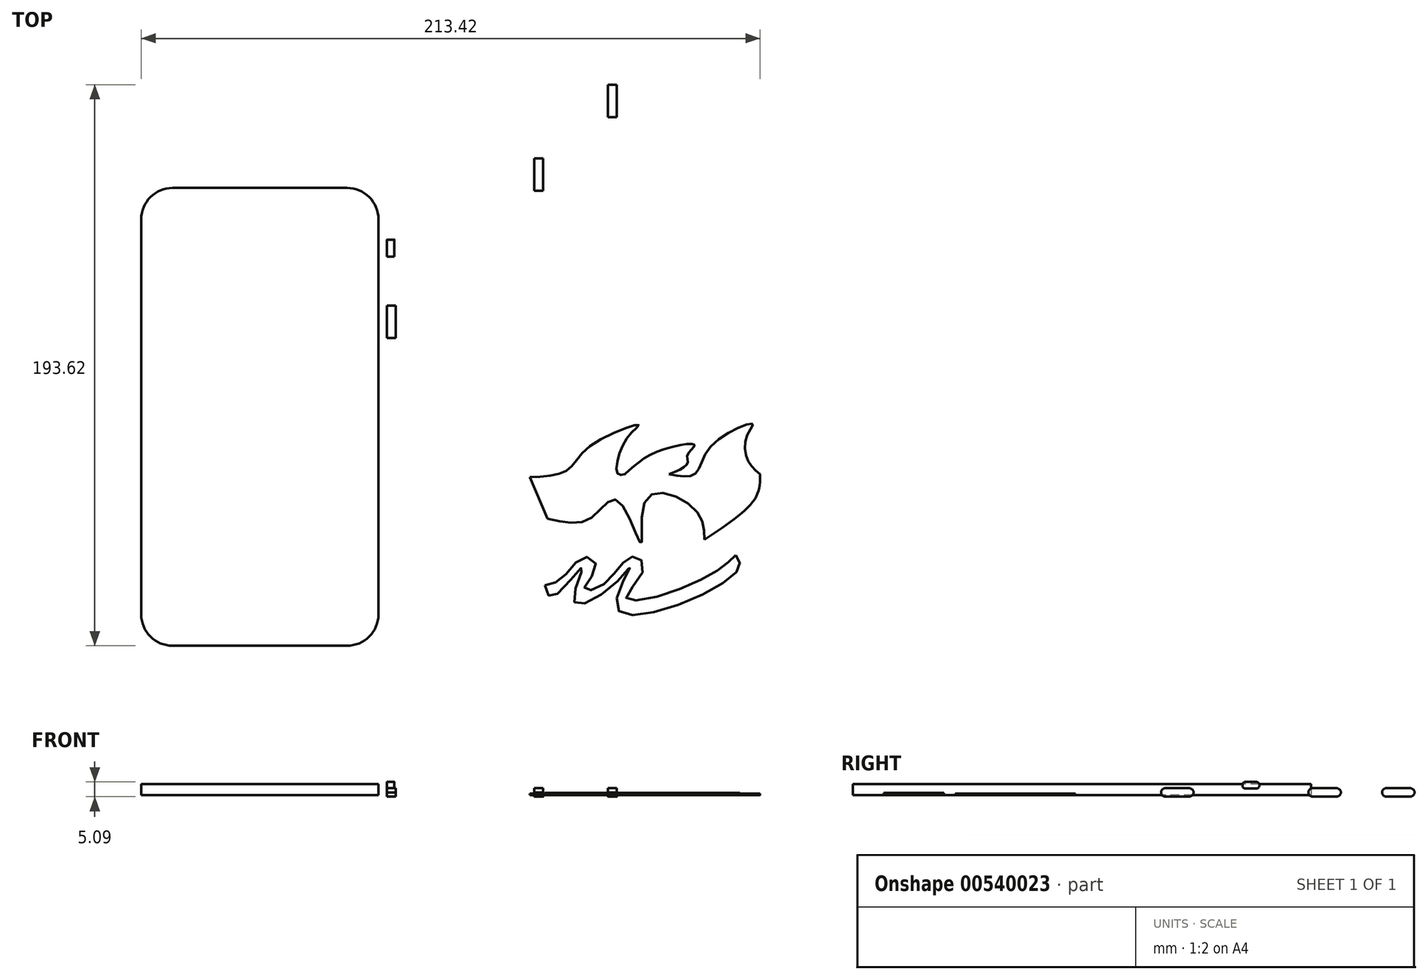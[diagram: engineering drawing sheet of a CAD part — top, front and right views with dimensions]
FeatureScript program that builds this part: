
annotation { "Feature Type Name" : "Feature", "Feature Type Description" : "" }
export const myFeature = defineFeature(function(context is Context, id is Id, definition is map)
    precondition{}
    {
        {
            var Q0;
            Q0=qCreatedBy(makeId("Right.planeOp"),FACE);
            var sketch = newSketch(context, id + "F0", { "sketchPlane" : qUnion([Q0])});
            skLineSegment(sketch, "E0.bottom", {"start": v(8.18, 2.37) * mm, "end": v(16.31, 2.37) * mm});
            skLineSegment(sketch, "E0.top", {"start": v(8.18, -0.57) * mm, "end": v(16.31, -0.57) * mm});
            skPoint(sketch, "E1.visualSharp", {"position": v(6.63, 2.37) * mm});
            skArc(sketch, "E1.filletArc", {"start": v(8.18, 2.37) * mm, "mid": v(7.09, 1.92) * mm, "end": v(6.63, 0.82) * mm});
            skPoint(sketch, "E2.visualSharp", {"position": v(17.86, 2.37) * mm});
            skArc(sketch, "E2.filletArc", {"start": v(17.86, 0.82) * mm, "mid": v(17.4, 1.92) * mm, "end": v(16.31, 2.37) * mm});
            skPoint(sketch, "E3.visualSharp", {"position": v(6.63, -0.57) * mm});
            skArc(sketch, "E3.filletArc", {"start": v(6.63, 0.98) * mm, "mid": v(7.09, -0.12) * mm, "end": v(8.18, -0.57) * mm});
            skPoint(sketch, "E4.visualSharp", {"position": v(17.86, -0.57) * mm});
            skArc(sketch, "E4.filletArc", {"start": v(16.31, -0.57) * mm, "mid": v(17.4, -0.12) * mm, "end": v(17.86, 0.98) * mm});
            skSolve(sketch);
        }
        {
            var Q0;
            Q0 = qSketchRegion(id + "F0", true);
            extrude(context, id + "F1", {"entities" : qUnion([Q0]), "depth" : 3.05 * mm, "offsetDistance" : 25.4 * mm});
        }
        {
            var Q0;
            Q0=makeQuery(id+"F1.opExtrude","SWEPT_BODY",BODY,{"disambiguationData":[OSD([sQuery(id+"F0.wireOp",EDGE,"E0.bottom"),sQuery(id+"F0.wireOp",EDGE,"E0.top"),sQuery(id+"F0.wireOp",EDGE,"E1.filletArc"),sQuery(id+"F0.wireOp",EDGE,"E2.filletArc"),sQuery(id+"F0.wireOp",EDGE,"E3.filletArc"),sQuery(id+"F0.wireOp",EDGE,"E4.filletArc")])]});
            transform(context, id + "F2", {"entities" : qUnion([Q0]), "transformType" : TransformType.TRANSLATION_3D, "dx" : 50.8 * mm, "dy" : 50.8 * mm, "dz" : 0 * mm, "makeCopy" : true});
        }
        {
            var Q0;
            Q0=makeQuery(id+"F2.opPattern","COPY",BODY,{"derivedFrom":makeQuery(id+"F1.opExtrude","SWEPT_BODY",BODY,{"disambiguationData":[OSD([sQuery(id+"F0.wireOp",EDGE,"E0.bottom"),sQuery(id+"F0.wireOp",EDGE,"E0.top"),sQuery(id+"F0.wireOp",EDGE,"E1.filletArc"),sQuery(id+"F0.wireOp",EDGE,"E2.filletArc"),sQuery(id+"F0.wireOp",EDGE,"E3.filletArc"),sQuery(id+"F0.wireOp",EDGE,"E4.filletArc")])]}),"instanceName":"1"});
            transform(context, id + "F3", {"entities" : qUnion([Q0]), "transformType" : TransformType.TRANSLATION_3D, "dx" : 25.4 * mm, "dy" : 25.4 * mm, "dz" : 0 * mm, "makeCopy" : true});
        }
        {
            var Q0;
            Q0=qCreatedBy(makeId("Right.planeOp"),FACE);
            var sketch = newSketch(context, id + "F4", { "sketchPlane" : qUnion([Q0])});
            skLineSegment(sketch, "E5.bottom", {"start": v(39.52, 4.52) * mm, "end": v(35.73, 4.52) * mm});
            skLineSegment(sketch, "E5.top", {"start": v(39.52, 2.26) * mm, "end": v(35.73, 2.26) * mm});
            skLineSegment(sketch, "E5.left", {"start": v(40.57, 3.48) * mm, "end": v(40.57, 3.3) * mm});
            skLineSegment(sketch, "E5.right", {"start": v(34.7, 3.48) * mm, "end": v(34.7, 3.3) * mm});
            skPoint(sketch, "E6.visualSharp", {"position": v(40.57, 4.52) * mm});
            skArc(sketch, "E6.filletArc", {"start": v(40.57, 3.48) * mm, "mid": v(40.26, 4.21) * mm, "end": v(39.52, 4.52) * mm});
            skPoint(sketch, "E7.visualSharp", {"position": v(34.7, 4.52) * mm});
            skArc(sketch, "E7.filletArc", {"start": v(35.73, 4.52) * mm, "mid": v(35, 4.21) * mm, "end": v(34.7, 3.48) * mm});
            skPoint(sketch, "E8.visualSharp", {"position": v(34.7, 2.26) * mm});
            skArc(sketch, "E8.filletArc", {"start": v(34.7, 3.3) * mm, "mid": v(35, 2.57) * mm, "end": v(35.73, 2.26) * mm});
            skPoint(sketch, "E9.visualSharp", {"position": v(40.57, 2.26) * mm});
            skArc(sketch, "E9.filletArc", {"start": v(39.52, 2.26) * mm, "mid": v(40.26, 2.57) * mm, "end": v(40.57, 3.3) * mm});
            skSolve(sketch);
        }
        {
            var Q0;
            Q0 = qSketchRegion(id + "F4", true);
            extrude(context, id + "F5", {"entities" : qUnion([Q0]), "depth" : 2.54 * mm, "offsetDistance" : 25.4 * mm});
        }
        {
            var Q0;
            Q0=qCreatedBy(makeId("Top.planeOp"),FACE);
            var sketch = newSketch(context, id + "F6", { "sketchPlane" : qUnion([Q0])});
            skLineSegment(sketch, "E10.bottom", {"start": v(-73.9, 58.43) * mm, "end": v(-13.76, 58.43) * mm});
            skLineSegment(sketch, "E10.top", {"start": v(-73.9, -99.56) * mm, "end": v(-13.76, -99.56) * mm});
            skLineSegment(sketch, "E10.left", {"start": v(-84.73, 47.6) * mm, "end": v(-84.73, -88.74) * mm});
            skLineSegment(sketch, "E10.right", {"start": v(-2.94, 47.6) * mm, "end": v(-2.94, -88.74) * mm});
            skPoint(sketch, "E11.visualSharp", {"position": v(-84.73, 58.43) * mm});
            skArc(sketch, "E11.filletArc", {"start": v(-73.9, 58.43) * mm, "mid": v(-81.56, 55.26) * mm, "end": v(-84.73, 47.6) * mm});
            skPoint(sketch, "E12.visualSharp", {"position": v(-2.94, 58.43) * mm});
            skArc(sketch, "E12.filletArc", {"start": v(-2.94, 47.6) * mm, "mid": v(-6.1, 55.26) * mm, "end": v(-13.76, 58.43) * mm});
            skPoint(sketch, "E13.visualSharp", {"position": v(-84.73, -99.56) * mm});
            skArc(sketch, "E13.filletArc", {"start": v(-84.73, -88.74) * mm, "mid": v(-81.56, -96.4) * mm, "end": v(-73.9, -99.56) * mm});
            skPoint(sketch, "E14.visualSharp", {"position": v(-2.94, -99.56) * mm});
            skArc(sketch, "E14.filletArc", {"start": v(-13.76, -99.56) * mm, "mid": v(-6.1, -96.4) * mm, "end": v(-2.94, -88.74) * mm});
            skSolve(sketch);
        }
        {
            var Q0;
            Q0 = qSketchRegion(id + "F6", true);
            extrude(context, id + "F7", {"entities" : qUnion([Q0]), "depth" : 3.8 * mm, "offsetDistance" : 25.4 * mm});
        }
        {
            var Q0;
            Q0=qCreatedBy(makeId("Top.planeOp"),FACE);
            var sketch = newSketch(context, id + "F8", { "sketchPlane" : qUnion([Q0])});
            skFitSpline(sketch, "E15", {"points": [v(49.21, -41.36) * mm, v(62.07, -39.04) * mm, v(69.9, -30.72) * mm, v(86.67, -23.35) * mm, v(84.57, -25.73) * mm, v(79.73, -34.67) * mm, v(79.7, -40.34) * mm, v(82.09, -40.36) * mm], "startDerivative": vector(83.32, 3.18) * mm, "endDerivative": vector(36.55, 9.2) * mm});
            skFitSpline(sketch, "E16", {"points": [v(82.09, -40.36) * mm, v(93.79, -32.36) * mm, v(106.05, -30.34) * mm, v(103.64, -33.61) * mm, v(103.62, -36.6) * mm, v(97.32, -40.36) * mm], "startDerivative": vector(34.64, 32.4) * mm, "endDerivative": vector(-44.46, -17.83) * mm});
            skFitSpline(sketch, "E17", {"points": [v(97.32, -40.36) * mm, v(106.05, -40.36) * mm, v(112.03, -30.34) * mm, v(126.12, -23) * mm, v(124.3, -26.57) * mm, v(124.25, -35.23) * mm, v(128.69, -40.36) * mm], "startDerivative": vector(62.09, -13) * mm, "endDerivative": vector(35.82, -29.98) * mm});
            skFitSpline(sketch, "E18", {"points": [v(55.4, -55.74) * mm, v(70.34, -55.53) * mm, v(79.34, -49.3) * mm, v(87.61, -64.3) * mm, v(89.8, -48.47) * mm, v(106.05, -52.46) * mm, v(109.43, -62.93) * mm], "startDerivative": vector(95.18, -22.86) * mm, "endDerivative": vector(1.3, -72.68) * mm});
            skFitSpline(sketch, "E19", {"points": [v(109.43, -62.93) * mm, v(126.95, -48.7) * mm, v(128.69, -40.36) * mm], "startDerivative": vector(35.62, 23.3) * mm, "endDerivative": vector(0.05, 21.7) * mm});
            skFitSpline(sketch, "E20", {"points": [v(55.4, -55.74) * mm, v(49.21, -41.36) * mm], "startDerivative": vector(-6.18, 14.38) * mm, "endDerivative": vector(-6.18, 14.38) * mm});
            skSolve(sketch);
        }
        {
            var Q0;
            Q0 = qSketchRegion(id + "F8", true);
            extrude(context, id + "F9", {"entities" : qUnion([Q0]), "depth" : 0.5 * mm, "offsetDistance" : 25.4 * mm});
        }
        {
            var Q0;
            Q0=qCreatedBy(makeId("Top.planeOp"),FACE);
            var sketch = newSketch(context, id + "F10", { "sketchPlane" : qUnion([Q0])});
            skFitSpline(sketch, "E21", {"points": [v(54.44, -78.75) * mm, v(60.63, -76.07) * mm, v(67.86, -68.98) * mm, v(72.08, -72.06) * mm, v(68.09, -79.85) * mm, v(73.14, -79.4) * mm, v(80.44, -72.01) * mm, v(85.53, -68.78) * mm, v(88.52, -73.14) * mm, v(82.5, -82.97) * mm, v(95.75, -81.82) * mm, v(115.56, -72.5) * mm, v(120.27, -68.26) * mm], "startDerivative": vector(87.17, 17.9) * mm, "endDerivative": vector(52.53, 56.1) * mm});
            skFitSpline(sketch, "E22", {"points": [v(54.44, -78.75) * mm, v(57.27, -82.6) * mm, v(67.42, -72.5) * mm, v(64.44, -84.09) * mm, v(76.68, -79.85) * mm, v(83.85, -72.5) * mm, v(79.07, -85.88) * mm, v(97.3, -86.48) * mm, v(121.5, -72.5) * mm, v(120.27, -68.26) * mm], "startDerivative": vector(23.92, -96.26) * mm, "endDerivative": vector(-42.27, 58.71) * mm});
            skSolve(sketch);
        }
        {
            var Q0;
            Q0 = qSketchRegion(id + "F10", true);
            extrude(context, id + "F11", {"entities" : qUnion([Q0]), "depth" : 0.76 * mm, "offsetDistance" : 25.4 * mm});
        }
    });
